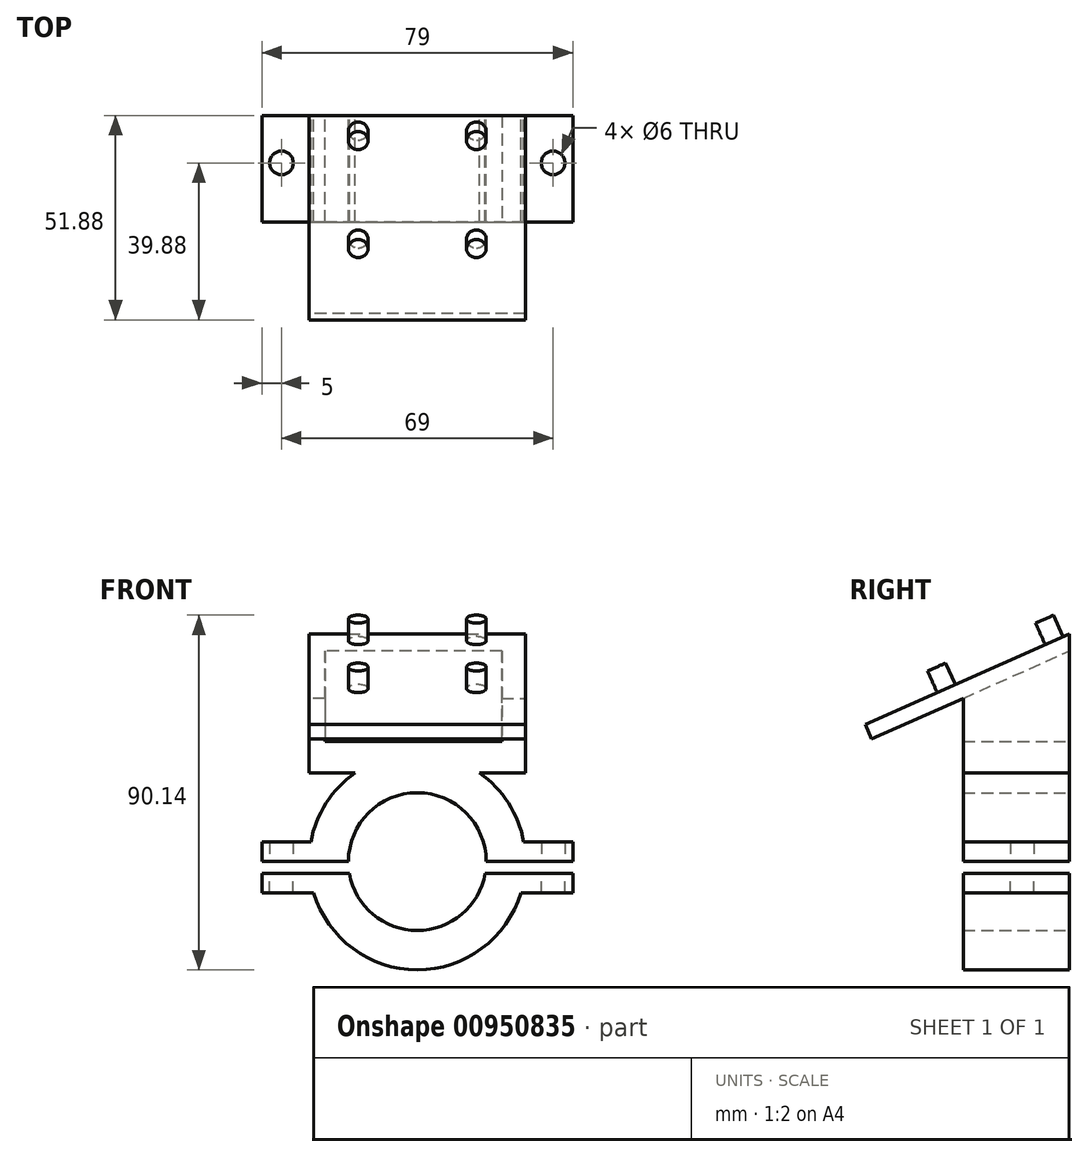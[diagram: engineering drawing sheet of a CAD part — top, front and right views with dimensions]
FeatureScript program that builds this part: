
annotation { "Feature Type Name" : "Feature", "Feature Type Description" : "" }
export const myFeature = defineFeature(function(context is Context, id is Id, definition is map)
    precondition{}
    {
        {
            var Q0;
            Q0=qCreatedBy(makeId("Front.planeOp"),FACE);
            var sketch = newSketch(context, id + "F0", { "sketchPlane" : qUnion([Q0])});
            skCircle(sketch, "E0", {"center": v(0, 0) * mm, "radius": 17.5 * mm});
            skCircle(sketch, "E1", {"center": v(0, 0) * mm, "radius": 27.5 * mm});
            skSolve(sketch);
        }
        {
            var Q0;
            Q0=makeQuery(id+"F0.imprint","IMPRINT",FACE,{"disambiguationData":[TD([[makeQuery(id+"F0.imprint","IMPRINT",EDGE,{"derivedFrom":sQuery(id+"F0.wireOp",EDGE,"E0")}),-1.0]])]});
            extrude(context, id + "F1", {"entities" : qUnion([Q0]), "depth" : 27 * mm, "offsetDistance" : 25 * mm});
        }
        {
            var Q0;
            Q0=makeQuery(id+"F1.opExtrude","CAP_FACE",FACE,{"disambiguationData":[OSD([sQuery(id+"F0.wireOp",EDGE,"E0"),sQuery(id+"F0.wireOp",EDGE,"E1")])],"isStart":false});
            var sketch = newSketch(context, id + "F2", { "sketchPlane" : qUnion([Q0])});
            skCircle(sketch, "E2.0", {"center": v(0, 0) * mm, "radius": 27.5 * mm});
            skLineSegment(sketch, "E3", {"start": v(-27.5, 27.5) * mm, "end": v(27.5, 27.5) * mm, "construction": true});
            skCircle(sketch, "E4.0", {"center": v(0, 0) * mm, "radius": 17.5 * mm});
            skPoint(sketch, "E5", {"position": v(0, 27.5) * mm});
            skLineSegment(sketch, "E6.0", {"start": v(-27.5, 22.5) * mm, "end": v(27.5, 22.5) * mm});
            skLineSegment(sketch, "E7", {"start": v(-27.5, 30.5) * mm, "end": v(-27.5, 22.5) * mm});
            skLineSegment(sketch, "E8", {"start": v(27.5, 30.5) * mm, "end": v(27.5, 22.5) * mm});
            skLineSegment(sketch, "E9.0", {"start": v(-27.5, 30.5) * mm, "end": v(27.5, 30.5) * mm});
            skSolve(sketch);
        }
        {
            var Q0;
            {var subQ5=sQuery(id+"F2.wireOp",EDGE,"E8");Q0=makeQuery(id+"F2.imprint","IMPRINT",FACE,{"disambiguationData":[TD([[makeQuery(id+"F2.imprint","IMPRINT",EDGE,{"derivedFrom":subQ5}),-1.0]])]});}
            var Q1;
            {var subQ0=sQuery(id+"F2.wireOp",EDGE,"E2.0");var subQ1=makeQuery(id+"F2.imprint","INTERSECT",VERTEX,{"derivedFrom":[subQ0,sQuery(id+"F2.wireOp",EDGE,"E3")]});Q1=makeQuery(id+"F2.imprint","IMPRINT",FACE,{"disambiguationData":[TD([[makeQuery(id+"F2.imprint","IMPRINT",EDGE,{"disambiguationData":[TD([[subQ1,1.0]])],"derivedFrom":subQ0}),1.0]])]});}
            var Q2;
            {var subQ5=sQuery(id+"F2.wireOp",EDGE,"E7");Q2=makeQuery(id+"F2.imprint","IMPRINT",FACE,{"disambiguationData":[TD([[makeQuery(id+"F2.imprint","IMPRINT",EDGE,{"derivedFrom":subQ5}),1.0]])]});}
            extrude(context, id + "F3", {"entities" : qUnion([Q0, Q1, Q2]), "operationType" : NewBodyOperationType.ADD, "oppositeDirection" : true, "depth" : 27 * mm, "offsetDistance" : 25 * mm});
        }
        {
            var Q0;
            Q0=makeQuery(id+"F3.opExtrude","SWEPT_FACE",FACE,{"disambiguationData":[OSD([sQuery(id+"F2.wireOp",EDGE,"E8")])]});
            var sketch = newSketch(context, id + "F4", { "sketchPlane" : qUnion([Q0])});
            skLineSegment(sketch, "E10.left", {"start": v(-27, 30.5) * mm, "end": v(-27, 41.5) * mm});
            skLineSegment(sketch, "E11.right", {"start": v(0, 53.5) * mm, "end": v(0, 30.5) * mm});
            skLineSegment(sketch, "E12", {"start": v(-27, 41.5) * mm, "end": v(0, 53.5) * mm});
            skSolve(sketch);
        }
        {
            var Q0;
            Q0 = qSketchRegion(id + "F4", true);
            var Q1;
            Q1=makeQuery(id+"F4.imprint","IMPRINT",FACE,{"disambiguationData":[TD([[makeQuery(id+"F4.imprint","IMPRINT",EDGE,{"derivedFrom":sQuery(id+"F4.wireOp",EDGE,"E10.left")}),-1.0]])]});
            extrude(context, id + "F5", {"entities" : qUnion([Q0, Q1]), "operationType" : NewBodyOperationType.ADD, "oppositeDirection" : true, "depth" : 6 * mm, "offsetDistance" : 25 * mm});
        }
        {
            var Q0;
            Q0=makeQuery(id+"F3.opExtrude","SWEPT_FACE",FACE,{"disambiguationData":[OSD([sQuery(id+"F2.wireOp",EDGE,"E7")])]});
            var sketch = newSketch(context, id + "F6", { "sketchPlane" : qUnion([Q0])});
            skLineSegment(sketch, "E13.0", {"start": v(0, 53.5) * mm, "end": v(0, 22.5) * mm});
            skPoint(sketch, "E14.0", {"position": v(13.5, 47.5) * mm});
            skLineSegment(sketch, "E15.0", {"start": v(0, 22.5) * mm, "end": v(27, 22.5) * mm});
            skPoint(sketch, "E16.0", {"position": v(27, 32) * mm});
            skLineSegment(sketch, "E17.0", {"start": v(27, 41.5) * mm, "end": v(27, 22.5) * mm});
            skLineSegment(sketch, "E18.0", {"start": v(27, 41.5) * mm, "end": v(0, 53.5) * mm});
            skSolve(sketch);
        }
        {
            var Q0;
            Q0 = qSketchRegion(id + "F6", true);
            extrude(context, id + "F7", {"entities" : qUnion([Q0]), "operationType" : NewBodyOperationType.ADD, "oppositeDirection" : true, "depth" : 4 * mm, "offsetDistance" : 25 * mm});
        }
        {
            var Q0;
            Q0=makeQuery(id+"F5.boolean.opBoolean","MERGE",FACE,{"derivedFrom":[makeQuery(id+"F3.boolean.opBoolean","MERGE",FACE,{"derivedFrom":[makeQuery(id+"F1.opExtrude","CAP_FACE",FACE,{"disambiguationData":[OSD([sQuery(id+"F0.wireOp",EDGE,"E0"),sQuery(id+"F0.wireOp",EDGE,"E1")])],"isStart":true}),makeQuery(id+"F3.opExtrude","CAP_FACE",FACE,{"disambiguationData":[OSD([sQuery(id+"F2.wireOp",EDGE,"E6.0"),sQuery(id+"F2.wireOp",EDGE,"E7"),sQuery(id+"F2.wireOp",EDGE,"E8"),sQuery(id+"F2.wireOp",EDGE,"E9.0")])],"isStart":false})]}),makeQuery(id+"F5.opExtrude","SWEPT_FACE",FACE,{"disambiguationData":[OSD([sQuery(id+"F4.wireOp",EDGE,"E11.right")])]})]});
            var sketch = newSketch(context, id + "F8", { "sketchPlane" : qUnion([Q0])});
            skLineSegment(sketch, "E19.bottom", {"start": v(-27.5, 0) * mm, "end": v(27.5, 0) * mm});
            skLineSegment(sketch, "E19.top", {"start": v(-27.5, -3) * mm, "end": v(27.5, -3) * mm});
            skLineSegment(sketch, "E19.left", {"start": v(-27.5, 0) * mm, "end": v(-27.5, -3) * mm});
            skLineSegment(sketch, "E19.right", {"start": v(27.5, 0) * mm, "end": v(27.5, -3) * mm});
            skPoint(sketch, "E20", {"position": v(0, -3) * mm});
            skSolve(sketch);
        }
        {
            var Q0;
            {var subQ0=sQuery(id+"F8.wireOp",EDGE,"E19.left");Q0=makeQuery(id+"F8.imprint","IMPRINT",FACE,{"disambiguationData":[TD([[makeQuery(id+"F8.imprint","IMPRINT",EDGE,{"derivedFrom":subQ0}),1.0]])]});}
            var Q1;
            {var subQ0=sQuery(id+"F8.wireOp",EDGE,"E19.right");Q1=makeQuery(id+"F8.imprint","IMPRINT",FACE,{"disambiguationData":[TD([[makeQuery(id+"F8.imprint","IMPRINT",EDGE,{"derivedFrom":subQ0}),-1.0]])]});}
            var Q2;
            {var subQ1=makeQuery(id+"F1.opExtrude","CAP_EDGE",EDGE,{"disambiguationData":[OSD([sQuery(id+"F0.wireOp",EDGE,"E1")])],"isStart":true});var subQ5=sQuery(id+"F8.wireOp",EDGE,"E19.top");var subQ6=makeQuery(id+"F8.imprint","INTERSECT",VERTEX,{"disambiguationData":[OD(0.0)],"derivedFrom":[subQ1,subQ5]});Q2=makeQuery(id+"F8.imprint","IMPRINT",FACE,{"disambiguationData":[TD([[makeQuery(id+"F8.imprint","IMPRINT",EDGE,{"disambiguationData":[TD([[subQ6,-1.0]])],"derivedFrom":subQ5}),1.0]])]});}
            var Q3;
            {var subQ1=makeQuery(id+"F1.opExtrude","CAP_EDGE",EDGE,{"disambiguationData":[OSD([sQuery(id+"F0.wireOp",EDGE,"E1")])],"isStart":true});var subQ5=sQuery(id+"F8.wireOp",EDGE,"E19.top");var subQ6=makeQuery(id+"F8.imprint","INTERSECT",VERTEX,{"disambiguationData":[OD(1.0)],"derivedFrom":[subQ1,subQ5]});Q3=makeQuery(id+"F8.imprint","IMPRINT",FACE,{"disambiguationData":[TD([[makeQuery(id+"F8.imprint","IMPRINT",EDGE,{"disambiguationData":[TD([[subQ6,1.0]])],"derivedFrom":subQ5}),1.0]])]});}
            extrude(context, id + "F9", {"entities" : qUnion([Q0, Q1, Q2, Q3]), "operationType" : NewBodyOperationType.REMOVE, "endBound" : BoundingType.THROUGH_ALL, "oppositeDirection" : true, "depth" : 25 * mm, "offsetDistance" : 25 * mm});
        }
        {
            var Q0;
            {var subQ0=sQuery(id+"F8.wireOp",EDGE,"E19.bottom");Q0=makeQuery(id+"F9.boolean.opBoolean","COPY",FACE,{"derivedFrom":makeQuery(id+"F9.opExtrude","SWEPT_FACE",FACE,{"disambiguationData":[OSD([subQ0]),TDD([makeQuery(id+"F8.imprint","IMPRINT",EDGE,{"disambiguationData":[TD([[makeQuery(id+"F8.imprint","INTERSECT",VERTEX,{"disambiguationData":[OD(0.0)],"derivedFrom":[makeQuery(id+"F1.opExtrude","CAP_EDGE",EDGE,{"disambiguationData":[OSD([sQuery(id+"F0.wireOp",EDGE,"E0")])],"isStart":true}),subQ0]}),1.0]])],"derivedFrom":subQ0})])]})});}
            var sketch = newSketch(context, id + "F10", { "sketchPlane" : qUnion([Q0])});
            skPoint(sketch, "E21.0", {"position": v(22.5, 27) * mm});
            skLineSegment(sketch, "E22.0", {"start": v(27.5, 27) * mm, "end": v(27.5, 0) * mm});
            skLineSegment(sketch, "E23.0", {"start": v(-27.5, 27) * mm, "end": v(-27.5, 0) * mm});
            skLineSegment(sketch, "E24.bottom", {"start": v(24.5, 27) * mm, "end": v(39.5, 27) * mm});
            skLineSegment(sketch, "E24.top", {"start": v(24.5, 0) * mm, "end": v(39.5, 0) * mm});
            skLineSegment(sketch, "E24.left", {"start": v(24.5, 27) * mm, "end": v(24.5, 0) * mm});
            skLineSegment(sketch, "E24.right", {"start": v(39.5, 27) * mm, "end": v(39.5, 0) * mm});
            skLineSegment(sketch, "E25.bottom", {"start": v(-24.5, 27) * mm, "end": v(-39.5, 27) * mm});
            skLineSegment(sketch, "E25.top", {"start": v(-24.5, 0) * mm, "end": v(-39.5, 0) * mm});
            skLineSegment(sketch, "E25.left", {"start": v(-24.5, 27) * mm, "end": v(-24.5, 0) * mm});
            skLineSegment(sketch, "E25.right", {"start": v(-39.5, 27) * mm, "end": v(-39.5, 0) * mm});
            skCircle(sketch, "E26", {"center": v(34.5, 12) * mm, "radius": 3 * mm});
            skCircle(sketch, "E27", {"center": v(-34.5, 12) * mm, "radius": 3 * mm});
            skSolve(sketch);
        }
        {
            var Q0;
            Q0 = qSketchRegion(id + "F10", true);
            extrude(context, id + "F11", {"entities" : qUnion([Q0]), "operationType" : NewBodyOperationType.ADD, "oppositeDirection" : true, "depth" : 5 * mm, "offsetDistance" : 25 * mm});
        }
        {
            var Q0;
            {var subQ0=sQuery(id+"F8.wireOp",EDGE,"E19.top");var subQ1=makeQuery(id+"F8.imprint","INTERSECT",VERTEX,{"disambiguationData":[OD(0.0)],"derivedFrom":[makeQuery(id+"F1.opExtrude","CAP_EDGE",EDGE,{"disambiguationData":[OSD([sQuery(id+"F0.wireOp",EDGE,"E1")])],"isStart":true}),subQ0]});Q0=makeQuery(id+"F9.boolean.opBoolean","COPY",FACE,{"derivedFrom":makeQuery(id+"F9.opExtrude","SWEPT_FACE",FACE,{"disambiguationData":[OSD([subQ0]),TDD([makeQuery(id+"F8.imprint","IMPRINT",EDGE,{"disambiguationData":[TD([[makeQuery(id+"F8.imprint","INTERSECT",VERTEX,{"derivedFrom":[subQ0,sQuery(id+"F8.wireOp",EDGE,"E19.left")]}),-1.0]])],"derivedFrom":subQ0}),makeQuery(id+"F8.imprint","IMPRINT",EDGE,{"disambiguationData":[TD([[subQ1,-1.0]])],"derivedFrom":subQ0})])]})});}
            var sketch = newSketch(context, id + "F12", { "sketchPlane" : qUnion([Q0])});
            skLineSegment(sketch, "E28.0", {"start": v(-39.5, -27) * mm, "end": v(-39.5, 0) * mm});
            skLineSegment(sketch, "E29.0", {"start": v(-39.5, -27) * mm, "end": v(-17.5, -27) * mm});
            skLineSegment(sketch, "E30.0", {"start": v(-17.5, 0) * mm, "end": v(-39.5, 0) * mm});
            skLineSegment(sketch, "E31.0.0", {"start": v(17.5, -27) * mm, "end": v(17.5, 0) * mm});
            skLineSegment(sketch, "E31.0.1", {"start": v(17.5, 0) * mm, "end": v(39.5, 0) * mm});
            skLineSegment(sketch, "E31.0.2", {"start": v(39.5, 0) * mm, "end": v(39.5, -27) * mm});
            skLineSegment(sketch, "E31.0.3", {"start": v(39.5, -27) * mm, "end": v(17.5, -27) * mm});
            skLineSegment(sketch, "E32.0.1", {"start": v(-39.5, 0) * mm, "end": v(-17.5, 0) * mm});
            skLineSegment(sketch, "E32.0.2", {"start": v(-17.5, 0) * mm, "end": v(-17.5, -27) * mm});
            skLineSegment(sketch, "E32.0.3", {"start": v(-17.5, -27) * mm, "end": v(-39.5, -27) * mm});
            skCircle(sketch, "E33.0", {"center": v(-34.5, -12) * mm, "radius": 3 * mm});
            skCircle(sketch, "E34.0", {"center": v(34.5, -12) * mm, "radius": 3 * mm});
            skSolve(sketch);
        }
        {
            var Q0;
            Q0 = qSketchRegion(id + "F12", true);
            extrude(context, id + "F13", {"entities" : qUnion([Q0]), "operationType" : NewBodyOperationType.ADD, "oppositeDirection" : true, "depth" : 5 * mm, "offsetDistance" : 25 * mm});
        }
        {
            var Q0;
            Q0=makeQuery(id+"F7.opExtrude","SWEPT_FACE",FACE,{"disambiguationData":[OSD([sQuery(id+"F6.wireOp",EDGE,"E18.0")])]});
            var sketch = newSketch(context, id + "F14", { "sketchPlane" : qUnion([Q0])});
            skLineSegment(sketch, "E35.top", {"start": v(-27.5, 21.73) * mm, "end": v(27.5, 21.73) * mm});
            skLineSegment(sketch, "E35.left", {"start": v(-27.5, -33.27) * mm, "end": v(-27.5, 21.73) * mm});
            skLineSegment(sketch, "E35.right", {"start": v(27.5, -33.27) * mm, "end": v(27.5, 21.73) * mm});
            skLineSegment(sketch, "E36.0", {"start": v(27.5, -7.82) * mm, "end": v(27.5, 21.73) * mm});
            skLineSegment(sketch, "E37", {"start": v(27.5, -33.27) * mm, "end": v(-27.5, -33.27) * mm});
            skSolve(sketch);
        }
        {
            var Q0;
            Q0 = qSketchRegion(id + "F14", true);
            extrude(context, id + "F15", {"entities" : qUnion([Q0]), "operationType" : NewBodyOperationType.ADD, "depth" : 4 * mm, "offsetDistance" : 25 * mm});
        }
        {
            var Q0;
            Q0=makeQuery(id+"F15.opExtrude","CAP_FACE",FACE,{"disambiguationData":[OSD([sQuery(id+"F14.wireOp",EDGE,"E35.bottom"),sQuery(id+"F14.wireOp",EDGE,"E35.top"),sQuery(id+"F14.wireOp",EDGE,"E35.left"),sQuery(id+"F14.wireOp",EDGE,"E35.right"),sQuery(id+"F14.wireOp",EDGE,"E36.0")])],"isStart":false});
            var sketch = newSketch(context, id + "F16", { "sketchPlane" : qUnion([Q0])});
            skLineSegment(sketch, "E38.bottom", {"start": v(-15, 19.23) * mm, "end": v(15, 19.23) * mm, "construction": true});
            skLineSegment(sketch, "E38.top", {"start": v(-15, -10.77) * mm, "end": v(15, -10.77) * mm, "construction": true});
            skLineSegment(sketch, "E38.left", {"start": v(-15, 19.23) * mm, "end": v(-15, -10.77) * mm, "construction": true});
            skLineSegment(sketch, "E38.right", {"start": v(15, 19.23) * mm, "end": v(15, -10.77) * mm, "construction": true});
            skLineSegment(sketch, "E39.0", {"start": v(-27.5, -7.82) * mm, "end": v(27.5, -7.82) * mm});
            skPoint(sketch, "E40", {"position": v(0, -10.77) * mm});
            skCircle(sketch, "E41", {"center": v(-15, -10.77) * mm, "radius": 2.5 * mm});
            skCircle(sketch, "E42", {"center": v(-15, 19.23) * mm, "radius": 2.5 * mm});
            skCircle(sketch, "E43", {"center": v(15, 19.23) * mm, "radius": 2.5 * mm});
            skCircle(sketch, "E44", {"center": v(15, -10.77) * mm, "radius": 2.5 * mm});
            skPoint(sketch, "E45", {"position": v(0, -33.27) * mm});
            skSolve(sketch);
        }
        {
            var Q0;
            Q0 = qSketchRegion(id + "F16", true);
            extrude(context, id + "F17", {"entities" : qUnion([Q0]), "operationType" : NewBodyOperationType.ADD, "depth" : 6 * mm, "offsetDistance" : 25 * mm});
        }
        {
            var Q0;
            {var subQ0=sQuery(id+"F2.wireOp",EDGE,"E8");Q0=makeQuery(id+"F15.boolean.opBoolean","MERGE",FACE,{"derivedFrom":[makeQuery(id+"F5.boolean.opBoolean","MERGE",FACE,{"derivedFrom":[makeQuery(id+"F3.opExtrude","SWEPT_FACE",FACE,{"disambiguationData":[OSD([subQ0])]}),makeQuery(id+"F5.opExtrude","CAP_FACE",FACE,{"disambiguationData":[OSD([subQ0,sQuery(id+"F2.wireOp",EDGE,"E9.0"),sQuery(id+"F4.wireOp",EDGE,"E10.left"),sQuery(id+"F4.wireOp",EDGE,"E11.right"),sQuery(id+"F4.wireOp",EDGE,"E12")])],"isStart":true})]}),makeQuery(id+"F15.opExtrude","SWEPT_FACE",FACE,{"disambiguationData":[OSD([sQuery(id+"F14.wireOp",EDGE,"E35.right"),sQuery(id+"F14.wireOp",EDGE,"E36.0")])]})]});}
            var sketch = newSketch(context, id + "F18", { "sketchPlane" : qUnion([Q0])});
            skLineSegment(sketch, "E46", {"start": v(-1.62, 57.16) * mm, "end": v(0, 53.5) * mm});
            skLineSegment(sketch, "E47.0", {"start": v(0, 57.88) * mm, "end": v(0, 22.5) * mm});
            skLineSegment(sketch, "E48.0", {"start": v(-51.88, 34.82) * mm, "end": v(0, 57.88) * mm});
            skPoint(sketch, "E49.orphan", {"position": v(-1.62, 57.16) * mm});
            skPoint(sketch, "E50.orphan", {"position": v(0, 53.5) * mm});
            skSolve(sketch);
        }
        {
            var Q0;
            Q0 = qSketchRegion(id + "F18", true);
            var Q1;
            Q1=makeQuery(id+"F15.boolean.opBoolean","MERGE",FACE,{"derivedFrom":[makeQuery(id+"F7.boolean.opBoolean","MERGE",FACE,{"derivedFrom":[makeQuery(id+"F3.opExtrude","SWEPT_FACE",FACE,{"disambiguationData":[OSD([sQuery(id+"F2.wireOp",EDGE,"E7")])]}),makeQuery(id+"F7.opExtrude","CAP_FACE",FACE,{"disambiguationData":[OSD([sQuery(id+"F6.wireOp",EDGE,"E13.0"),sQuery(id+"F6.wireOp",EDGE,"E15.0"),sQuery(id+"F6.wireOp",EDGE,"E17.0"),sQuery(id+"F6.wireOp",EDGE,"E18.0")])],"isStart":true})]}),makeQuery(id+"F15.opExtrude","SWEPT_FACE",FACE,{"disambiguationData":[OSD([sQuery(id+"F14.wireOp",EDGE,"E35.left")])]})]});
            extrude(context, id + "F19", {"entities" : qUnion([Q0]), "operationType" : NewBodyOperationType.ADD, "endBound" : BoundingType.UP_TO_SURFACE, "oppositeDirection" : true, "depth" : 25 * mm, "endBoundEntityFace" : qUnion([Q1]), "offsetDistance" : 25 * mm});
        }
    });
